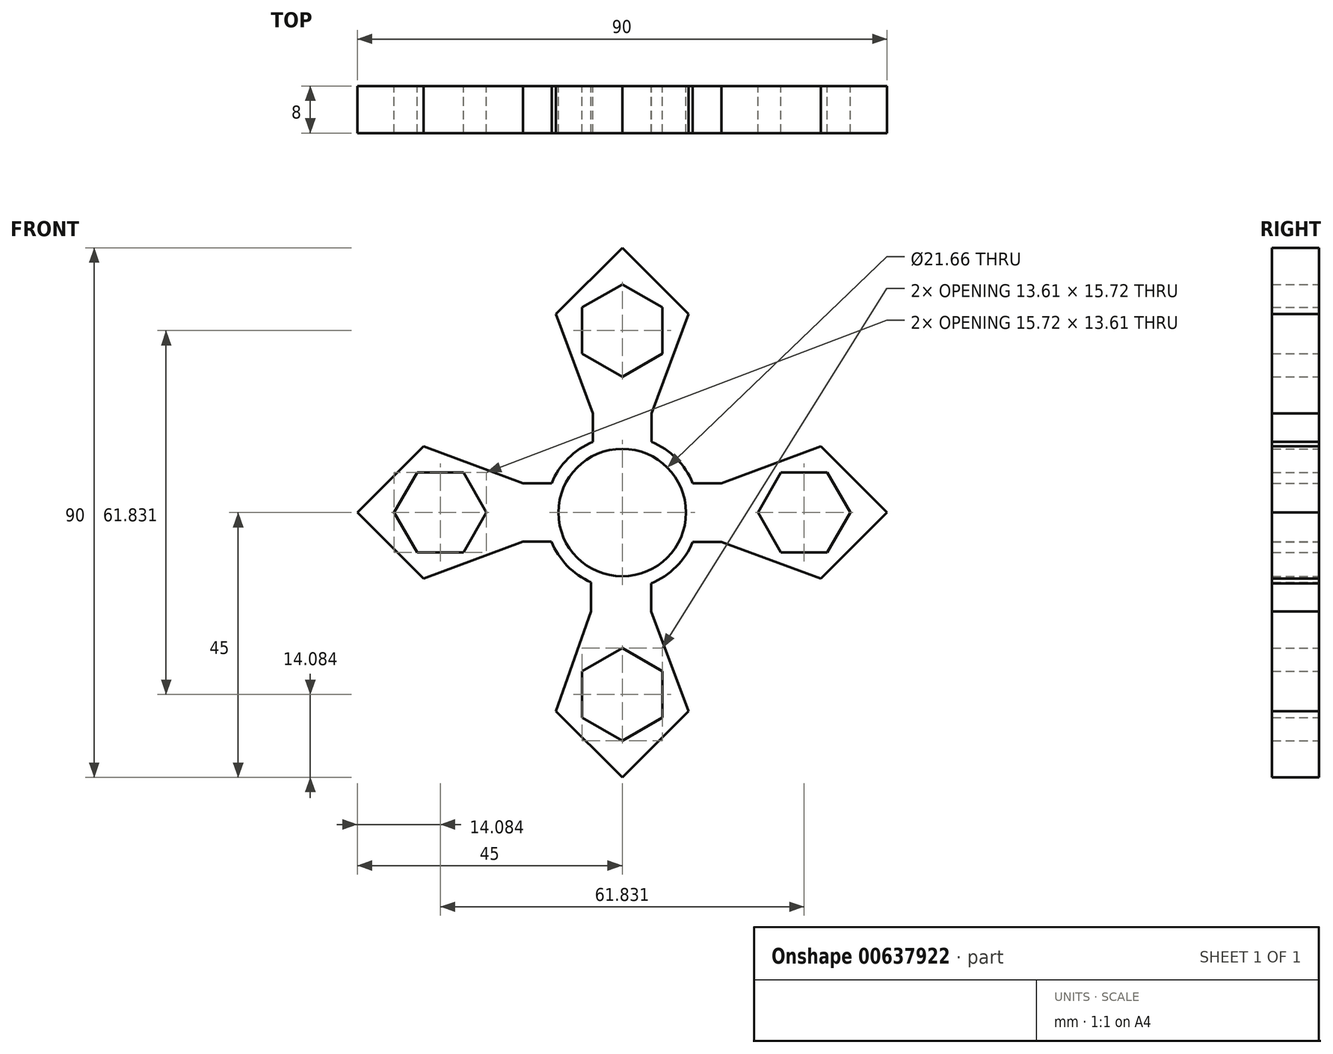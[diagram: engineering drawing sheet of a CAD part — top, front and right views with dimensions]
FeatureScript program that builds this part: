
annotation { "Feature Type Name" : "Feature", "Feature Type Description" : "" }
export const myFeature = defineFeature(function(context is Context, id is Id, definition is map)
    precondition{}
    {
        {
            var Q0;
            Q0=qCreatedBy(makeId("Front.planeOp"),FACE);
            var sketch = newSketch(context, id + "F0", { "sketchPlane" : qUnion([Q0])});
            skCircle(sketch, "E0", {"center": v(0, 0) * mm, "radius": 10.83 * mm});
            skLineSegment(sketch, "E1.bottom", {"start": v(45, -45) * mm, "end": v(-45, -45) * mm});
            skLineSegment(sketch, "E1.top", {"start": v(45, 45) * mm, "end": v(-45, 45) * mm});
            skLineSegment(sketch, "E1.left", {"start": v(45, -45) * mm, "end": v(45, 45) * mm});
            skLineSegment(sketch, "E1.right", {"start": v(-45, -45) * mm, "end": v(-45, 45) * mm});
            skLineSegment(sketch, "E2", {"start": v(0, 45) * mm, "end": v(0, 0) * mm});
            skLineSegment(sketch, "E3", {"start": v(0, -45) * mm, "end": v(0, 0) * mm});
            skLineSegment(sketch, "E4", {"start": v(45, 0) * mm, "end": v(0, 0) * mm});
            skLineSegment(sketch, "E5", {"start": v(0, 0) * mm, "end": v(-45, 0) * mm});
            skLineSegment(sketch, "E6", {"start": v(0, 0) * mm, "end": v(45, 45) * mm});
            skLineSegment(sketch, "E7", {"start": v(0, 0) * mm, "end": v(45, -45) * mm});
            skLineSegment(sketch, "E8", {"start": v(0, 0) * mm, "end": v(-45, -45) * mm});
            skLineSegment(sketch, "E9", {"start": v(0, 0) * mm, "end": v(-45, 45) * mm});
            skLineSegment(sketch, "E10", {"start": v(0, -10.83) * mm, "end": v(0, -16.83) * mm});
            skLineSegment(sketch, "E11", {"start": v(0, -16.83) * mm, "end": v(4.92, -16.83) * mm});
            skLineSegment(sketch, "E12", {"start": v(4.92, -16.83) * mm, "end": v(-5.3, -16.83) * mm});
            skLineSegment(sketch, "E13", {"start": v(-5.3, -16.83) * mm, "end": v(-5.3, -9.45) * mm});
            skLineSegment(sketch, "E14", {"start": v(4.92, -16.83) * mm, "end": v(4.92, -9.65) * mm});
            skLineSegment(sketch, "E15", {"start": v(10.83, 0) * mm, "end": v(16.83, 0) * mm});
            skLineSegment(sketch, "E16", {"start": v(16.83, 0) * mm, "end": v(16.83, -5) * mm});
            skLineSegment(sketch, "E17", {"start": v(16.83, -5) * mm, "end": v(16.83, 5) * mm});
            skLineSegment(sketch, "E18", {"start": v(16.83, 5) * mm, "end": v(9.6, 5) * mm});
            skLineSegment(sketch, "E19", {"start": v(16.83, -5) * mm, "end": v(9.6, -5) * mm});
            skLineSegment(sketch, "E20", {"start": v(22.5, 22.5) * mm, "end": v(45, 0) * mm});
            skLineSegment(sketch, "E21", {"start": v(45, 0) * mm, "end": v(22.5, -22.5) * mm});
            skLineSegment(sketch, "E22", {"start": v(22.5, -22.5) * mm, "end": v(0, -45) * mm});
            skLineSegment(sketch, "E23", {"start": v(-22.5, -22.5) * mm, "end": v(0, -45) * mm});
            skLineSegment(sketch, "E24", {"start": v(-45, 0) * mm, "end": v(-22.5, -22.5) * mm});
            skLineSegment(sketch, "E25", {"start": v(-45, 0) * mm, "end": v(-22.5, 22.5) * mm});
            skLineSegment(sketch, "E26", {"start": v(-22.5, 22.5) * mm, "end": v(0, 45) * mm});
            skLineSegment(sketch, "E27", {"start": v(22.5, 22.5) * mm, "end": v(0, 45) * mm});
            skLineSegment(sketch, "E28", {"start": v(-10.83, 0) * mm, "end": v(-16.83, 0) * mm});
            skLineSegment(sketch, "E29", {"start": v(-16.83, 0) * mm, "end": v(-16.83, 5) * mm});
            skLineSegment(sketch, "E30", {"start": v(-16.83, 5) * mm, "end": v(-16.83, -4.92) * mm});
            skLineSegment(sketch, "E31", {"start": v(-16.83, -4.92) * mm, "end": v(-9.65, -4.92) * mm});
            skLineSegment(sketch, "E32", {"start": v(-16.83, 5) * mm, "end": v(-9.6, 5) * mm});
            skLineSegment(sketch, "E33", {"start": v(0, 10.83) * mm, "end": v(0, 16.83) * mm});
            skLineSegment(sketch, "E34", {"start": v(0, 16.83) * mm, "end": v(5, 16.83) * mm});
            skLineSegment(sketch, "E35", {"start": v(5, 16.83) * mm, "end": v(-5, 16.83) * mm});
            skLineSegment(sketch, "E36", {"start": v(-5, 16.83) * mm, "end": v(-5, 9.6) * mm});
            skLineSegment(sketch, "E37", {"start": v(5, 16.83) * mm, "end": v(5, 9.6) * mm});
            skLineSegment(sketch, "E38", {"start": v(-16.83, 5) * mm, "end": v(-33.75, 11.25) * mm});
            skLineSegment(sketch, "E39", {"start": v(-33.75, 11.25) * mm, "end": v(-45, 0) * mm});
            skLineSegment(sketch, "E40", {"start": v(-16.83, -4.92) * mm, "end": v(-33.75, -11.25) * mm});
            skLineSegment(sketch, "E41", {"start": v(-33.75, -11.25) * mm, "end": v(-45, 0) * mm});
            skLineSegment(sketch, "E42", {"start": v(5, 16.83) * mm, "end": v(11.25, 33.75) * mm});
            skLineSegment(sketch, "E43", {"start": v(11.25, 33.75) * mm, "end": v(0, 45) * mm});
            skLineSegment(sketch, "E44", {"start": v(-5, 16.83) * mm, "end": v(-11.25, 33.75) * mm});
            skLineSegment(sketch, "E45", {"start": v(-11.25, 33.75) * mm, "end": v(0, 45) * mm});
            skLineSegment(sketch, "E46", {"start": v(16.83, 5) * mm, "end": v(33.75, 11.25) * mm});
            skLineSegment(sketch, "E47", {"start": v(33.75, 11.25) * mm, "end": v(45, 0) * mm});
            skLineSegment(sketch, "E48", {"start": v(16.83, -5) * mm, "end": v(33.75, -11.25) * mm});
            skLineSegment(sketch, "E49", {"start": v(33.75, -11.25) * mm, "end": v(45, 0) * mm});
            skLineSegment(sketch, "E50", {"start": v(4.92, -16.83) * mm, "end": v(11.25, -33.75) * mm});
            skLineSegment(sketch, "E51", {"start": v(11.25, -33.75) * mm, "end": v(0, -45) * mm});
            skLineSegment(sketch, "E52", {"start": v(-5.3, -16.83) * mm, "end": v(-11.25, -33.75) * mm});
            skLineSegment(sketch, "E53", {"start": v(-11.25, -33.75) * mm, "end": v(0, -45) * mm});
            skCircle(sketch, "E54", {"center": v(0, 0) * mm, "radius": 13 * mm});
            skLineSegment(sketch, "E55", {"start": v(0, -16.83) * mm, "end": v(0, -45) * mm});
            skLineSegment(sketch, "E56", {"start": v(0, -30.92) * mm, "end": v(10.2, -30.92) * mm});
            skLineSegment(sketch, "E57", {"start": v(10.2, -30.92) * mm, "end": v(-10.25, -30.92) * mm});
            skLineSegment(sketch, "E58", {"start": v(16.83, 0) * mm, "end": v(45, 0) * mm});
            skLineSegment(sketch, "E59", {"start": v(30.92, 0) * mm, "end": v(30.92, 10.2) * mm});
            skLineSegment(sketch, "E60", {"start": v(30.92, 10.2) * mm, "end": v(30.92, -10.2) * mm});
            skLineSegment(sketch, "E61", {"start": v(0, 16.83) * mm, "end": v(0, 45) * mm});
            skLineSegment(sketch, "E62", {"start": v(0, 30.92) * mm, "end": v(10.2, 30.92) * mm});
            skLineSegment(sketch, "E63", {"start": v(10.2, 30.92) * mm, "end": v(-10.2, 30.92) * mm});
            skLineSegment(sketch, "E64", {"start": v(-16.83, 0) * mm, "end": v(-45, 0) * mm});
            skLineSegment(sketch, "E65", {"start": v(-30.92, 0) * mm, "end": v(-30.92, 10.2) * mm});
            skLineSegment(sketch, "E66", {"start": v(-30.92, 10.2) * mm, "end": v(-30.92, -10.2) * mm});
            skCircle(sketch, "E67.cCircle", {"center": v(-30.92, 0) * mm, "radius": 6.8 * mm, "construction": true});
            skLineSegment(sketch, "E67.0", {"start": v(-34.85, 6.8) * mm, "end": v(-26.99, 6.8) * mm});
            skLineSegment(sketch, "E67.1", {"start": v(-26.99, 6.8) * mm, "end": v(-23.06, 0) * mm});
            skLineSegment(sketch, "E67.2", {"start": v(-23.06, 0) * mm, "end": v(-26.99, -6.8) * mm});
            skLineSegment(sketch, "E67.3", {"start": v(-26.99, -6.8) * mm, "end": v(-34.85, -6.8) * mm});
            skLineSegment(sketch, "E67.4", {"start": v(-34.85, -6.8) * mm, "end": v(-38.78, 0) * mm});
            skLineSegment(sketch, "E67.5", {"start": v(-38.78, 0) * mm, "end": v(-34.85, 6.8) * mm});
            skPoint(sketch, "E67.0.midPoint", {"position": v(-30.92, 6.8) * mm});
            skCircle(sketch, "E68.cCircle", {"center": v(30.92, 0) * mm, "radius": 6.8 * mm, "construction": true});
            skLineSegment(sketch, "E68.0", {"start": v(26.99, 6.8) * mm, "end": v(34.85, 6.8) * mm});
            skLineSegment(sketch, "E68.1", {"start": v(34.85, 6.8) * mm, "end": v(38.78, 0) * mm});
            skLineSegment(sketch, "E68.2", {"start": v(38.78, 0) * mm, "end": v(34.85, -6.8) * mm});
            skLineSegment(sketch, "E68.3", {"start": v(34.85, -6.8) * mm, "end": v(26.99, -6.8) * mm});
            skLineSegment(sketch, "E68.4", {"start": v(26.99, -6.8) * mm, "end": v(23.06, 0) * mm});
            skLineSegment(sketch, "E68.5", {"start": v(23.06, 0) * mm, "end": v(26.99, 6.8) * mm});
            skPoint(sketch, "E68.0.midPoint", {"position": v(30.92, 6.8) * mm});
            skCircle(sketch, "E69.cCircle", {"center": v(0, 30.92) * mm, "radius": 6.8 * mm, "construction": true});
            skLineSegment(sketch, "E69.0", {"start": v(6.8, 34.85) * mm, "end": v(6.8, 26.99) * mm});
            skLineSegment(sketch, "E69.1", {"start": v(6.8, 26.99) * mm, "end": v(0, 23.06) * mm});
            skLineSegment(sketch, "E69.2", {"start": v(0, 23.06) * mm, "end": v(-6.8, 26.99) * mm});
            skLineSegment(sketch, "E69.3", {"start": v(-6.8, 26.99) * mm, "end": v(-6.8, 34.85) * mm});
            skLineSegment(sketch, "E69.4", {"start": v(-6.8, 34.85) * mm, "end": v(0, 38.78) * mm});
            skLineSegment(sketch, "E69.5", {"start": v(0, 38.78) * mm, "end": v(6.8, 34.85) * mm});
            skPoint(sketch, "E69.0.midPoint", {"position": v(6.8, 30.92) * mm});
            skCircle(sketch, "E70.cCircle", {"center": v(0, -30.92) * mm, "radius": 6.8 * mm, "construction": true});
            skLineSegment(sketch, "E70.0", {"start": v(6.8, -26.99) * mm, "end": v(6.8, -34.85) * mm});
            skLineSegment(sketch, "E70.1", {"start": v(6.8, -34.85) * mm, "end": v(0, -38.78) * mm});
            skLineSegment(sketch, "E70.2", {"start": v(0, -38.78) * mm, "end": v(-6.8, -34.85) * mm});
            skLineSegment(sketch, "E70.3", {"start": v(-6.8, -34.85) * mm, "end": v(-6.8, -26.99) * mm});
            skLineSegment(sketch, "E70.4", {"start": v(-6.8, -26.99) * mm, "end": v(0, -23.06) * mm});
            skLineSegment(sketch, "E70.5", {"start": v(0, -23.06) * mm, "end": v(6.8, -26.99) * mm});
            skPoint(sketch, "E70.0.midPoint", {"position": v(6.8, -30.92) * mm});
            skSolve(sketch);
        }
        {
            var Q0;
            {var subQ4=sQuery(id+"F0.wireOp",EDGE,"E42");Q0=makeQuery(id+"F0.imprint","IMPRINT",FACE,{"disambiguationData":[TD([[makeQuery(id+"F0.imprint","IMPRINT",EDGE,{"derivedFrom":subQ4}),1.0]])]});}
            var Q1;
            {var subQ4=sQuery(id+"F0.wireOp",EDGE,"E44");Q1=makeQuery(id+"F0.imprint","IMPRINT",FACE,{"disambiguationData":[TD([[makeQuery(id+"F0.imprint","IMPRINT",EDGE,{"derivedFrom":subQ4}),-1.0]])]});}
            var Q2;
            {var subQ4=sQuery(id+"F0.wireOp",EDGE,"E50");Q2=makeQuery(id+"F0.imprint","IMPRINT",FACE,{"disambiguationData":[TD([[makeQuery(id+"F0.imprint","IMPRINT",EDGE,{"derivedFrom":subQ4}),-1.0]])]});}
            var Q3;
            {var subQ4=sQuery(id+"F0.wireOp",EDGE,"E52");Q3=makeQuery(id+"F0.imprint","IMPRINT",FACE,{"disambiguationData":[TD([[makeQuery(id+"F0.imprint","IMPRINT",EDGE,{"derivedFrom":subQ4}),1.0]])]});}
            var Q4;
            {var subQ4=sQuery(id+"F0.wireOp",EDGE,"E48");Q4=makeQuery(id+"F0.imprint","IMPRINT",FACE,{"disambiguationData":[TD([[makeQuery(id+"F0.imprint","IMPRINT",EDGE,{"derivedFrom":subQ4}),1.0]])]});}
            var Q5;
            {var subQ4=sQuery(id+"F0.wireOp",EDGE,"E46");Q5=makeQuery(id+"F0.imprint","IMPRINT",FACE,{"disambiguationData":[TD([[makeQuery(id+"F0.imprint","IMPRINT",EDGE,{"derivedFrom":subQ4}),-1.0]])]});}
            var Q6;
            {var subQ4=sQuery(id+"F0.wireOp",EDGE,"E38");Q6=makeQuery(id+"F0.imprint","IMPRINT",FACE,{"disambiguationData":[TD([[makeQuery(id+"F0.imprint","IMPRINT",EDGE,{"derivedFrom":subQ4}),1.0]])]});}
            var Q7;
            {var subQ4=sQuery(id+"F0.wireOp",EDGE,"E40");Q7=makeQuery(id+"F0.imprint","IMPRINT",FACE,{"disambiguationData":[TD([[makeQuery(id+"F0.imprint","IMPRINT",EDGE,{"derivedFrom":subQ4}),-1.0]])]});}
            var Q8;
            {var subQ1=sQuery(id+"F0.wireOp",EDGE,"E10");var subQ3=sQuery(id+"F0.wireOp",EDGE,"E54");var subQ4=makeQuery(id+"F0.imprint","INTERSECT",VERTEX,{"derivedFrom":[subQ1,subQ3]});Q8=makeQuery(id+"F0.imprint","IMPRINT",FACE,{"disambiguationData":[TD([[makeQuery(id+"F0.imprint","IMPRINT",EDGE,{"disambiguationData":[TD([[subQ4,1.0]])],"derivedFrom":subQ3}),-1.0]])]});}
            var Q9;
            {var subQ1=sQuery(id+"F0.wireOp",EDGE,"E10");var subQ3=sQuery(id+"F0.wireOp",EDGE,"E54");var subQ4=makeQuery(id+"F0.imprint","INTERSECT",VERTEX,{"derivedFrom":[subQ1,subQ3]});Q9=makeQuery(id+"F0.imprint","IMPRINT",FACE,{"disambiguationData":[TD([[makeQuery(id+"F0.imprint","IMPRINT",EDGE,{"disambiguationData":[TD([[subQ4,-1.0]])],"derivedFrom":subQ3}),-1.0]])]});}
            var Q10;
            {var subQ1=sQuery(id+"F0.wireOp",EDGE,"E0");var subQ3=sQuery(id+"F0.wireOp",EDGE,"E14");var subQ4=makeQuery(id+"F0.imprint","INTERSECT",VERTEX,{"derivedFrom":[subQ1,subQ3]});Q10=makeQuery(id+"F0.imprint","IMPRINT",FACE,{"disambiguationData":[TD([[makeQuery(id+"F0.imprint","IMPRINT",EDGE,{"disambiguationData":[TD([[subQ4,1.0]])],"derivedFrom":subQ3}),1.0]])]});}
            var Q11;
            {var subQ1=sQuery(id+"F0.wireOp",EDGE,"E0");var subQ3=sQuery(id+"F0.wireOp",EDGE,"E13");var subQ4=makeQuery(id+"F0.imprint","INTERSECT",VERTEX,{"derivedFrom":[subQ1,subQ3]});Q11=makeQuery(id+"F0.imprint","IMPRINT",FACE,{"disambiguationData":[TD([[makeQuery(id+"F0.imprint","IMPRINT",EDGE,{"disambiguationData":[TD([[subQ4,1.0]])],"derivedFrom":subQ3}),-1.0]])]});}
            var Q12;
            {var subQ0=sQuery(id+"F0.wireOp",EDGE,"E13");var subQ1=sQuery(id+"F0.wireOp",EDGE,"E0");var subQ2=makeQuery(id+"F0.imprint","INTERSECT",VERTEX,{"derivedFrom":[subQ1,subQ0]});Q12=makeQuery(id+"F0.imprint","IMPRINT",FACE,{"disambiguationData":[TD([[makeQuery(id+"F0.imprint","IMPRINT",EDGE,{"disambiguationData":[TD([[subQ2,1.0]])],"derivedFrom":subQ1}),-1.0]])]});}
            var Q13;
            {var subQ0=sQuery(id+"F0.wireOp",EDGE,"E31");var subQ1=sQuery(id+"F0.wireOp",EDGE,"E0");var subQ2=makeQuery(id+"F0.imprint","INTERSECT",VERTEX,{"derivedFrom":[subQ1,subQ0]});Q13=makeQuery(id+"F0.imprint","IMPRINT",FACE,{"disambiguationData":[TD([[makeQuery(id+"F0.imprint","IMPRINT",EDGE,{"disambiguationData":[TD([[subQ2,-1.0]])],"derivedFrom":subQ1}),-1.0]])]});}
            var Q14;
            {var subQ1=sQuery(id+"F0.wireOp",EDGE,"E0");var subQ3=sQuery(id+"F0.wireOp",EDGE,"E31");var subQ4=makeQuery(id+"F0.imprint","INTERSECT",VERTEX,{"derivedFrom":[subQ1,subQ3]});Q14=makeQuery(id+"F0.imprint","IMPRINT",FACE,{"disambiguationData":[TD([[makeQuery(id+"F0.imprint","IMPRINT",EDGE,{"disambiguationData":[TD([[subQ4,1.0]])],"derivedFrom":subQ3}),1.0]])]});}
            var Q15;
            {var subQ1=sQuery(id+"F0.wireOp",EDGE,"E28");var subQ3=sQuery(id+"F0.wireOp",EDGE,"E54");var subQ4=makeQuery(id+"F0.imprint","INTERSECT",VERTEX,{"derivedFrom":[subQ1,subQ3]});Q15=makeQuery(id+"F0.imprint","IMPRINT",FACE,{"disambiguationData":[TD([[makeQuery(id+"F0.imprint","IMPRINT",EDGE,{"disambiguationData":[TD([[subQ4,-1.0]])],"derivedFrom":subQ3}),-1.0]])]});}
            var Q16;
            {var subQ1=sQuery(id+"F0.wireOp",EDGE,"E28");var subQ3=sQuery(id+"F0.wireOp",EDGE,"E54");var subQ4=makeQuery(id+"F0.imprint","INTERSECT",VERTEX,{"derivedFrom":[subQ1,subQ3]});Q16=makeQuery(id+"F0.imprint","IMPRINT",FACE,{"disambiguationData":[TD([[makeQuery(id+"F0.imprint","IMPRINT",EDGE,{"disambiguationData":[TD([[subQ4,1.0]])],"derivedFrom":subQ3}),-1.0]])]});}
            var Q17;
            {var subQ1=sQuery(id+"F0.wireOp",EDGE,"E0");var subQ3=sQuery(id+"F0.wireOp",EDGE,"E32");var subQ4=makeQuery(id+"F0.imprint","INTERSECT",VERTEX,{"derivedFrom":[subQ1,subQ3]});Q17=makeQuery(id+"F0.imprint","IMPRINT",FACE,{"disambiguationData":[TD([[makeQuery(id+"F0.imprint","IMPRINT",EDGE,{"disambiguationData":[TD([[subQ4,1.0]])],"derivedFrom":subQ3}),-1.0]])]});}
            var Q18;
            {var subQ0=sQuery(id+"F0.wireOp",EDGE,"E32");var subQ1=sQuery(id+"F0.wireOp",EDGE,"E0");var subQ2=makeQuery(id+"F0.imprint","INTERSECT",VERTEX,{"derivedFrom":[subQ1,subQ0]});Q18=makeQuery(id+"F0.imprint","IMPRINT",FACE,{"disambiguationData":[TD([[makeQuery(id+"F0.imprint","IMPRINT",EDGE,{"disambiguationData":[TD([[subQ2,1.0]])],"derivedFrom":subQ1}),-1.0]])]});}
            var Q19;
            {var subQ0=sQuery(id+"F0.wireOp",EDGE,"E36");var subQ1=sQuery(id+"F0.wireOp",EDGE,"E0");var subQ2=makeQuery(id+"F0.imprint","INTERSECT",VERTEX,{"derivedFrom":[subQ1,subQ0]});Q19=makeQuery(id+"F0.imprint","IMPRINT",FACE,{"disambiguationData":[TD([[makeQuery(id+"F0.imprint","IMPRINT",EDGE,{"disambiguationData":[TD([[subQ2,-1.0]])],"derivedFrom":subQ1}),-1.0]])]});}
            var Q20;
            {var subQ1=sQuery(id+"F0.wireOp",EDGE,"E33");var subQ3=sQuery(id+"F0.wireOp",EDGE,"E54");var subQ4=makeQuery(id+"F0.imprint","INTERSECT",VERTEX,{"derivedFrom":[subQ1,subQ3]});Q20=makeQuery(id+"F0.imprint","IMPRINT",FACE,{"disambiguationData":[TD([[makeQuery(id+"F0.imprint","IMPRINT",EDGE,{"disambiguationData":[TD([[subQ4,1.0]])],"derivedFrom":subQ3}),-1.0]])]});}
            var Q21;
            {var subQ1=sQuery(id+"F0.wireOp",EDGE,"E0");var subQ3=sQuery(id+"F0.wireOp",EDGE,"E36");var subQ4=makeQuery(id+"F0.imprint","INTERSECT",VERTEX,{"derivedFrom":[subQ1,subQ3]});Q21=makeQuery(id+"F0.imprint","IMPRINT",FACE,{"disambiguationData":[TD([[makeQuery(id+"F0.imprint","IMPRINT",EDGE,{"disambiguationData":[TD([[subQ4,1.0]])],"derivedFrom":subQ3}),1.0]])]});}
            var Q22;
            {var subQ1=sQuery(id+"F0.wireOp",EDGE,"E0");var subQ3=sQuery(id+"F0.wireOp",EDGE,"E37");var subQ4=makeQuery(id+"F0.imprint","INTERSECT",VERTEX,{"derivedFrom":[subQ1,subQ3]});Q22=makeQuery(id+"F0.imprint","IMPRINT",FACE,{"disambiguationData":[TD([[makeQuery(id+"F0.imprint","IMPRINT",EDGE,{"disambiguationData":[TD([[subQ4,1.0]])],"derivedFrom":subQ3}),-1.0]])]});}
            var Q23;
            {var subQ0=sQuery(id+"F0.wireOp",EDGE,"E37");var subQ1=sQuery(id+"F0.wireOp",EDGE,"E0");var subQ2=makeQuery(id+"F0.imprint","INTERSECT",VERTEX,{"derivedFrom":[subQ1,subQ0]});Q23=makeQuery(id+"F0.imprint","IMPRINT",FACE,{"disambiguationData":[TD([[makeQuery(id+"F0.imprint","IMPRINT",EDGE,{"disambiguationData":[TD([[subQ2,1.0]])],"derivedFrom":subQ1}),-1.0]])]});}
            var Q24;
            {var subQ0=sQuery(id+"F0.wireOp",EDGE,"E18");var subQ1=sQuery(id+"F0.wireOp",EDGE,"E0");var subQ2=makeQuery(id+"F0.imprint","INTERSECT",VERTEX,{"derivedFrom":[subQ1,subQ0]});Q24=makeQuery(id+"F0.imprint","IMPRINT",FACE,{"disambiguationData":[TD([[makeQuery(id+"F0.imprint","IMPRINT",EDGE,{"disambiguationData":[TD([[subQ2,-1.0]])],"derivedFrom":subQ1}),-1.0]])]});}
            var Q25;
            {var subQ1=sQuery(id+"F0.wireOp",EDGE,"E0");var subQ3=sQuery(id+"F0.wireOp",EDGE,"E18");var subQ4=makeQuery(id+"F0.imprint","INTERSECT",VERTEX,{"derivedFrom":[subQ1,subQ3]});Q25=makeQuery(id+"F0.imprint","IMPRINT",FACE,{"disambiguationData":[TD([[makeQuery(id+"F0.imprint","IMPRINT",EDGE,{"disambiguationData":[TD([[subQ4,1.0]])],"derivedFrom":subQ3}),1.0]])]});}
            var Q26;
            {var subQ0=sQuery(id+"F0.wireOp",EDGE,"E14");var subQ1=sQuery(id+"F0.wireOp",EDGE,"E0");var subQ2=makeQuery(id+"F0.imprint","INTERSECT",VERTEX,{"derivedFrom":[subQ1,subQ0]});Q26=makeQuery(id+"F0.imprint","IMPRINT",FACE,{"disambiguationData":[TD([[makeQuery(id+"F0.imprint","IMPRINT",EDGE,{"disambiguationData":[TD([[subQ2,-1.0]])],"derivedFrom":subQ1}),-1.0]])]});}
            var Q27;
            {var subQ1=sQuery(id+"F0.wireOp",EDGE,"E15");var subQ3=sQuery(id+"F0.wireOp",EDGE,"E54");var subQ4=makeQuery(id+"F0.imprint","INTERSECT",VERTEX,{"derivedFrom":[subQ1,subQ3]});Q27=makeQuery(id+"F0.imprint","IMPRINT",FACE,{"disambiguationData":[TD([[makeQuery(id+"F0.imprint","IMPRINT",EDGE,{"disambiguationData":[TD([[subQ4,-1.0]])],"derivedFrom":subQ3}),-1.0]])]});}
            var Q28;
            {var subQ1=sQuery(id+"F0.wireOp",EDGE,"E33");var subQ3=sQuery(id+"F0.wireOp",EDGE,"E54");var subQ4=makeQuery(id+"F0.imprint","INTERSECT",VERTEX,{"derivedFrom":[subQ1,subQ3]});Q28=makeQuery(id+"F0.imprint","IMPRINT",FACE,{"disambiguationData":[TD([[makeQuery(id+"F0.imprint","IMPRINT",EDGE,{"disambiguationData":[TD([[subQ4,-1.0]])],"derivedFrom":subQ3}),-1.0]])]});}
            var Q29;
            {var subQ1=sQuery(id+"F0.wireOp",EDGE,"E15");var subQ3=sQuery(id+"F0.wireOp",EDGE,"E54");var subQ4=makeQuery(id+"F0.imprint","INTERSECT",VERTEX,{"derivedFrom":[subQ1,subQ3]});Q29=makeQuery(id+"F0.imprint","IMPRINT",FACE,{"disambiguationData":[TD([[makeQuery(id+"F0.imprint","IMPRINT",EDGE,{"disambiguationData":[TD([[subQ4,1.0]])],"derivedFrom":subQ3}),-1.0]])]});}
            var Q30;
            {var subQ1=sQuery(id+"F0.wireOp",EDGE,"E0");var subQ3=sQuery(id+"F0.wireOp",EDGE,"E19");var subQ4=makeQuery(id+"F0.imprint","INTERSECT",VERTEX,{"derivedFrom":[subQ1,subQ3]});Q30=makeQuery(id+"F0.imprint","IMPRINT",FACE,{"disambiguationData":[TD([[makeQuery(id+"F0.imprint","IMPRINT",EDGE,{"disambiguationData":[TD([[subQ4,1.0]])],"derivedFrom":subQ3}),-1.0]])]});}
            var Q31;
            {var subQ0=sQuery(id+"F0.wireOp",EDGE,"E19");var subQ1=sQuery(id+"F0.wireOp",EDGE,"E0");var subQ2=makeQuery(id+"F0.imprint","INTERSECT",VERTEX,{"derivedFrom":[subQ1,subQ0]});Q31=makeQuery(id+"F0.imprint","IMPRINT",FACE,{"disambiguationData":[TD([[makeQuery(id+"F0.imprint","IMPRINT",EDGE,{"disambiguationData":[TD([[subQ2,1.0]])],"derivedFrom":subQ1}),-1.0]])]});}
            extrude(context, id + "F1", {"entities" : qUnion([Q0, Q1, Q2, Q3, Q4, Q5, Q6, Q7, Q8, Q9, Q10, Q11, Q12, Q13, Q14, Q15, Q16, Q17, Q18, Q19, Q20, Q21, Q22, Q23, Q24, Q25, Q26, Q27, Q28, Q29, Q30, Q31]), "depth" : 8 * mm, "offsetDistance" : 25 * mm});
        }
    });
